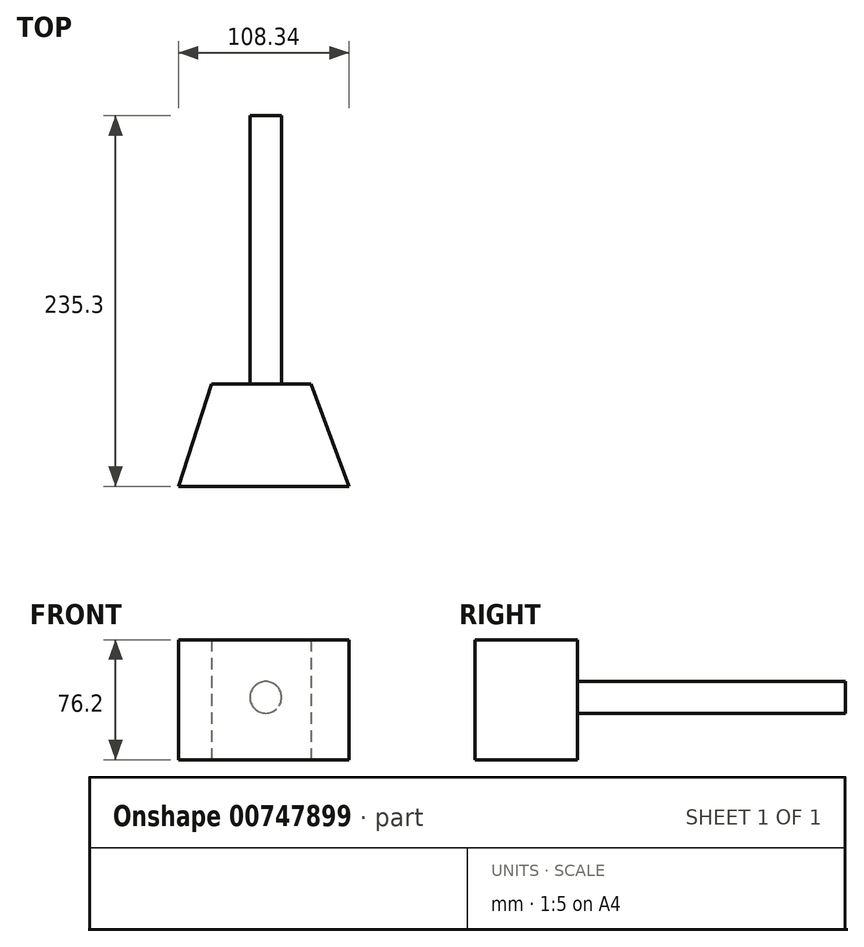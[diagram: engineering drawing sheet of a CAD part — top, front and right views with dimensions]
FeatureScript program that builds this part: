
annotation { "Feature Type Name" : "Feature", "Feature Type Description" : "" }
export const myFeature = defineFeature(function(context is Context, id is Id, definition is map)
    precondition{}
    {
        {
            var Q0;
            Q0=qCreatedBy(makeId("Top.planeOp"),FACE);
            var sketch = newSketch(context, id + "F0", { "sketchPlane" : qUnion([Q0])});
            skLineSegment(sketch, "E0.bottom", {"start": v(-55.35, 32.8) * mm, "end": v(52.99, 32.8) * mm});
            skLineSegment(sketch, "E0.top", {"start": v(-55.35, -32.1) * mm, "end": v(52.99, -32.1) * mm});
            skLineSegment(sketch, "E0.left", {"start": v(-55.35, 32.8) * mm, "end": v(-55.35, -32.1) * mm});
            skLineSegment(sketch, "E0.right", {"start": v(52.99, 32.8) * mm, "end": v(52.99, -32.1) * mm});
            skLineSegment(sketch, "E1", {"start": v(-55.35, -32.1) * mm, "end": v(-34.58, 32.8) * mm});
            skLineSegment(sketch, "E2", {"start": v(52.99, -32.1) * mm, "end": v(28.68, 32.8) * mm});
            skSolve(sketch);
        }
        {
            var Q0;
            Q0=makeQuery(id+"F0.imprint","IMPRINT",FACE,{"disambiguationData":[TD([[makeQuery(id+"F0.imprint","IMPRINT",EDGE,{"derivedFrom":sQuery(id+"F0.wireOp",EDGE,"E0.top")}),1.0]])]});
            extrude(context, id + "F1", {"entities" : qUnion([Q0]), "depth" : 25.4 * mm, "offsetDistance" : 25.4 * mm});
        }
        {
            var Q0;
            Q0=makeQuery(id+"F1.opExtrude","CAP_FACE",FACE,{"disambiguationData":[OSD([sQuery(id+"F0.wireOp",EDGE,"E0.bottom"),sQuery(id+"F0.wireOp",EDGE,"E0.top"),sQuery(id+"F0.wireOp",EDGE,"E1"),sQuery(id+"F0.wireOp",EDGE,"E2")])],"isStart":true});
            extrude(context, id + "F2", {"entities" : qUnion([Q0]), "operationType" : NewBodyOperationType.ADD, "depth" : 50.8 * mm, "offsetDistance" : 25.4 * mm});
        }
        {
            var Q0;
            Q0=qCreatedBy(makeId("Front.planeOp"),FACE);
            var sketch = newSketch(context, id + "F3", { "sketchPlane" : qUnion([Q0])});
            skCircle(sketch, "E3", {"center": v(0, -11.2) * mm, "radius": 10.05 * mm});
            skSolve(sketch);
        }
        {
            var Q0;
            Q0 = qSketchRegion(id + "F3", true);
            extrude(context, id + "F4", {"entities" : qUnion([Q0]), "operationType" : NewBodyOperationType.ADD, "depth" : -203.2 * mm, "offsetDistance" : 25.4 * mm});
        }
        {
            var Q0;
            Q0=qCreatedBy(makeId("Front.planeOp"),FACE);
            var sketch = newSketch(context, id + "F5", { "sketchPlane" : qUnion([Q0])});
            skLineSegment(sketch, "E4.bottom", {"start": v(13.41, -15.28) * mm, "end": v(-11.6, -15.28) * mm});
            skLineSegment(sketch, "E4.top", {"start": v(13.41, -2.72) * mm, "end": v(-11.6, -2.72) * mm});
            skLineSegment(sketch, "E4.left", {"start": v(13.41, -15.28) * mm, "end": v(13.41, -2.72) * mm});
            skLineSegment(sketch, "E4.right", {"start": v(-11.6, -15.28) * mm, "end": v(-11.6, -2.72) * mm});
            skSolve(sketch);
        }
        {
            var Q0;
            Q0=sQuery(id+"F5.wireOp",EDGE,"E4.bottom");
            extrude(context, id + "F6", {"bodyType" : ToolBodyType.SURFACE, "surfaceEntities" : qUnion([Q0]), "depth" : 38.1 * mm, "offsetDistance" : 25.4 * mm});
        }
    });
